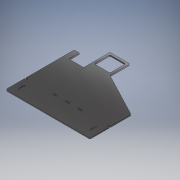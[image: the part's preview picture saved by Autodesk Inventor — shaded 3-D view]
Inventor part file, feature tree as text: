
AUTODESK INVENTOR PART (.ipt)
format: ipt  version: 2018 (Build 220112000, 112)  size: 247,296 bytes
history: native  units: mm
features: extrude x3, sketch x3, fillet x2, other x1
ambient origin geometry x8: Origin, YZ Plane, XZ Plane, XY Plane, X Axis, Y Axis, Z Axis, Center Point
bodies: Body1 (feature_tree)
feature tree (9):
  other  "Sólido1"
  extrude  "Extrusión1"  Depth=20.0mm
  fillet  "Empalme1"  Radius=25.0mm
  fillet  "Empalme2"  Radius=50.0mm
  extrude  "Extrusión2"  Depth=2.0mm
  extrude  "Extrusión3"  Depth=6.0mm TaperAngle=0.0deg
  sketch  "Boceto1"  dims[d0=305.0mm d1=95.0mm d2=95.0mm d3=195.0mm d4=400.0mm d7=75.0mm d8=75.0mm d9=20.0mm d10=25.0mm d11=50.0mm]
  sketch  "Boceto2"  dims[d12=6.0mm d13=0.0mm d14=2.0mm]
  sketch  "Boceto3"  dims[d15=6.0mm d16=20.0mm d17=6.0mm d18=20.0mm d19=60.0mm d20=20.0mm d21=60.0mm d22=8.0mm d23=20.0mm d24=6.0mm d25=110.0mm d27=6.0mm d28=6.0mm d29=107.0mm d31=6.0mm d32=0.0mm d33=70.0mm d34=10.0mm d35=20.0mm d36=6.0mm d38=20.0mm d39=60.0mm d40=20.0mm d41=60.0mm d42=8.0mm d43=20.0mm d44=6.0mm d45=110.0mm d46=6.0mm d47=20.0mm d48=12.0mm d49=6.0mm d50=44.0mm d51=6.0mm d52=6.0mm d54=6.0mm d55=6.0mm d56=26.0mm d57=8.0mm d58=8.0mm d59=6.0mm d60=0.0mm]
